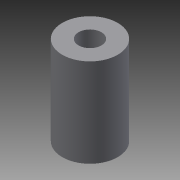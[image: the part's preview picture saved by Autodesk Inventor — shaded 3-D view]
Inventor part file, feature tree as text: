
AUTODESK INVENTOR PART (.ipt)
format: ipt  version: 2015 (Build 190159000, 159)  size: 72,192 bytes
history: native  units: in
note: dims shown in document units (in); Inventor stores cm internally (conversion verified against a paired STEP export)
features: extrude x1, sketch x1
ambient origin geometry x8: Origin, YZ Plane, XZ Plane, XY Plane, X Axis, Y Axis, Z Axis, Center Point
bodies: Solid1 (feature_tree)
feature tree (2):
  extrude  "Extrusion1"  Depth=0.4724in
  sketch  "Sketch1"  dims[d0=0.122in d1=0.2953in d2=0.4724in d3=0.0in]
